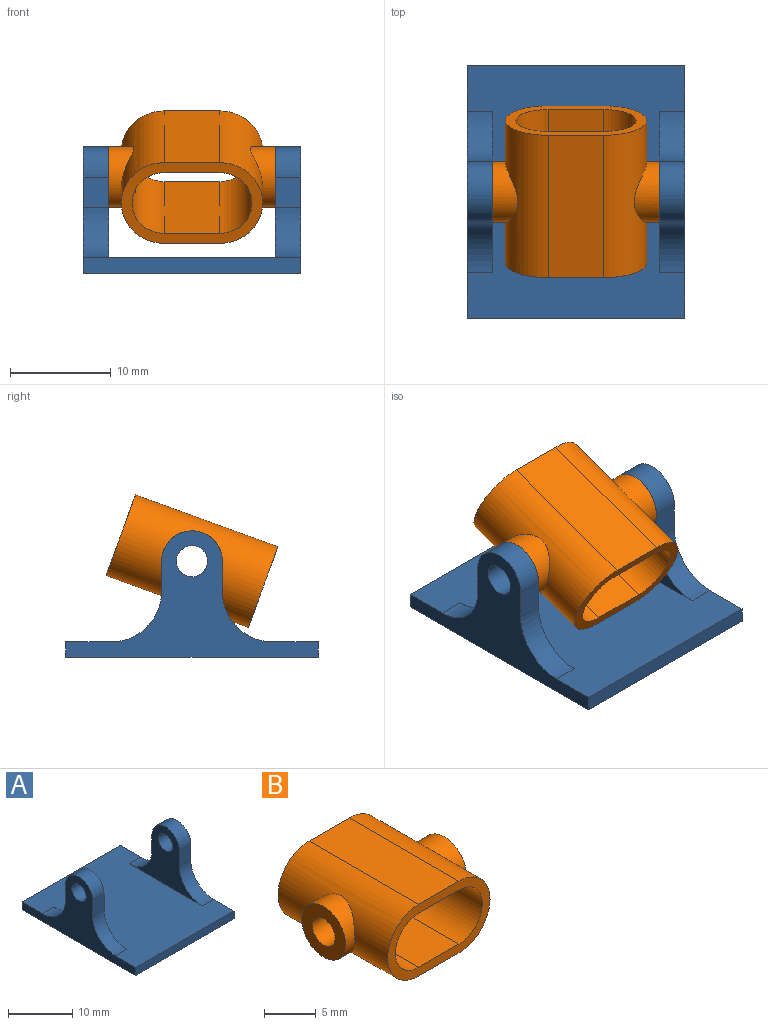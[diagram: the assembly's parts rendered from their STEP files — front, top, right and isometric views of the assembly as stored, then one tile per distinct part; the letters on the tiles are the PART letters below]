
ASSEMBLY  parts=2 mates=1
PART A: 20 faces, bbox 21.5x25x12.5 mm
  f0: plane 3x2.5mm, normal (0,1,0), area 7.5mm2, adj f1,f4,f14,f19
  f1: cylinder r=3mm len=6mm, axis (-1,0,0), area 23.6mm2, adj f0,f2,f14,f19
  f2: plane 3x2.5mm, normal (0,-1,0), area 7.5mm2, adj f1,f5,f14,f19
  f3: cylinder r=1.55mm len=3.1mm, axis (-1,0,0), area 24.3mm2, adj f14,f19
  f4: cylinder r=5mm len=5mm, axis (1,0,0), area 19.6mm2, adj f0,f13,f14,f19
  f5: cylinder r=5mm len=5mm, axis (-1,0,0), area 19.6mm2, adj f2,f13,f14,f19
  f6: plane 21.5x1.5mm, normal (0,-1,0), area 32.2mm2, adj f7,f13,f14,f15
  f7: plane 25x21.5mm, normal (0,0,-1), area 537.5mm2, adj f6,f8,f14,f15
  f8: plane 21.5x1.5mm, normal (0,1,0), area 32.2mm2, adj f7,f13,f14,f15
  f9: plane 3x2.5mm, normal (0,1,0), area 7.5mm2, adj f10,f15,f16,f18
  f10: cylinder r=3mm len=6mm, axis (-1,0,0), area 23.6mm2, adj f9,f11,f15,f18
  f11: plane 3x2.5mm, normal (0,-1,0), area 7.5mm2, adj f10,f15,f17,f18
  f12: cylinder r=1.55mm len=3.1mm, axis (-1,0,0), area 24.3mm2, adj f15,f18
  f13: plane 25x21.5mm, normal (0,0,1), area 457.5mm2, adj f4,f5,f6,f8,f14,f15,f16,f17
  f14: plane 25x12.5mm, normal (1,0,0), area 102.8mm2, adj f0,f1,f2,f3,f4,f5,f6,f7
  f15: plane 25x12.5mm, normal (-1,0,0), area 102.8mm2, adj f6,f7,f8,f9,f10,f11,f12,f13
  f16: cylinder r=5mm len=5mm, axis (1,0,0), area 19.6mm2, adj f9,f13,f15,f18
  f17: cylinder r=5mm len=5mm, axis (-1,0,0), area 19.6mm2, adj f11,f13,f15,f18
  f18: plane 16x11mm, normal (1,0,0), area 65.3mm2, adj f9,f10,f11,f12,f13,f16,f17
  f19: plane 16x11mm, normal (-1,0,0), area 65.3mm2, adj f0,f1,f2,f3,f4,f5,f13
PART B: 16 faces, bbox 16.5x15x8.5 mm
  f0: cylinder r=1.55mm len=3.1mm, axis (-1,0,0), area 24.3mm2, adj f4,f11
  f1: cylinder r=4.25mm len=15mm, axis (0,1,0), area 169.8mm2, adj f5,f8,f9,f10,f14
  f2: cylinder r=4.25mm len=15mm, axis (0,1,0), area 169.8mm2, adj f5,f8,f9,f10,f12
  f3: cylinder r=3.2mm len=15mm, axis (0,1,0), area 143mm2, adj f6,f7,f9,f10,f13
  f4: cylinder r=3.2mm len=15mm, axis (0,1,0), area 143mm2, adj f0,f6,f7,f9,f10
  f5: plane 15x5.5mm, normal (0,0,-1), area 82.5mm2, adj f1,f2,f9,f10
  f6: plane 15x5.5mm, normal (0,0,1), area 82.5mm2, adj f3,f4,f9,f10
  f7: plane 15x5.5mm, normal (0,0,-1), area 82.5mm2, adj f3,f4,f9,f10
  f8: plane 15x5.5mm, normal (0,0,1), area 82.5mm2, adj f1,f2,f9,f10
  f9: plane 14x8.5mm, normal (0,-1,0), area 36.1mm2, adj f1,f2,f3,f4,f5,f6,f7,f8
  f10: plane 14x8.5mm, normal (0,1,0), area 36.1mm2, adj f1,f2,f3,f4,f5,f6,f7,f8
  f11: plane 6x6mm, normal (1,0,0), area 20.7mm2, adj f0,f12
  f12: cylinder r=3mm len=6mm, axis (-1,0,0), area 34.7mm2, adj f2,f11
  f13: cylinder r=1.55mm len=3.1mm, axis (-1,0,0), area 24.3mm2, adj f3,f15
  f14: cylinder r=3mm len=6mm, axis (-1,0,0), area 34.7mm2, adj f1,f15
  f15: plane 6x6mm, normal (-1,0,0), area 20.7mm2, adj f13,f14
PLACE A at identity fixed
PLACE B rot(axis=(-1,0,0),160deg) t=(0,0,0)mm
MATE revolute B.f0 <-> A.f1  axis (-1,0,0) through (-8.25,0,0)mm
